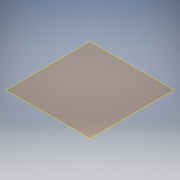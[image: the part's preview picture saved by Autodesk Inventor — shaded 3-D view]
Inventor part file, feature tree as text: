
AUTODESK INVENTOR PART (.ipt)
format: ipt  version: 2016 (Build 200138000, 138)  size: 76,800 bytes
history: native  units: in
note: dims shown in document units (in); Inventor stores cm internally (conversion verified against a paired STEP export)
features: plane x1
ambient origin geometry x8: Origin, YZ Plane, XZ Plane, XY Plane, X Axis, Y Axis, Z Axis, Center Point
feature tree (1):
  plane  "Work Plane1"
